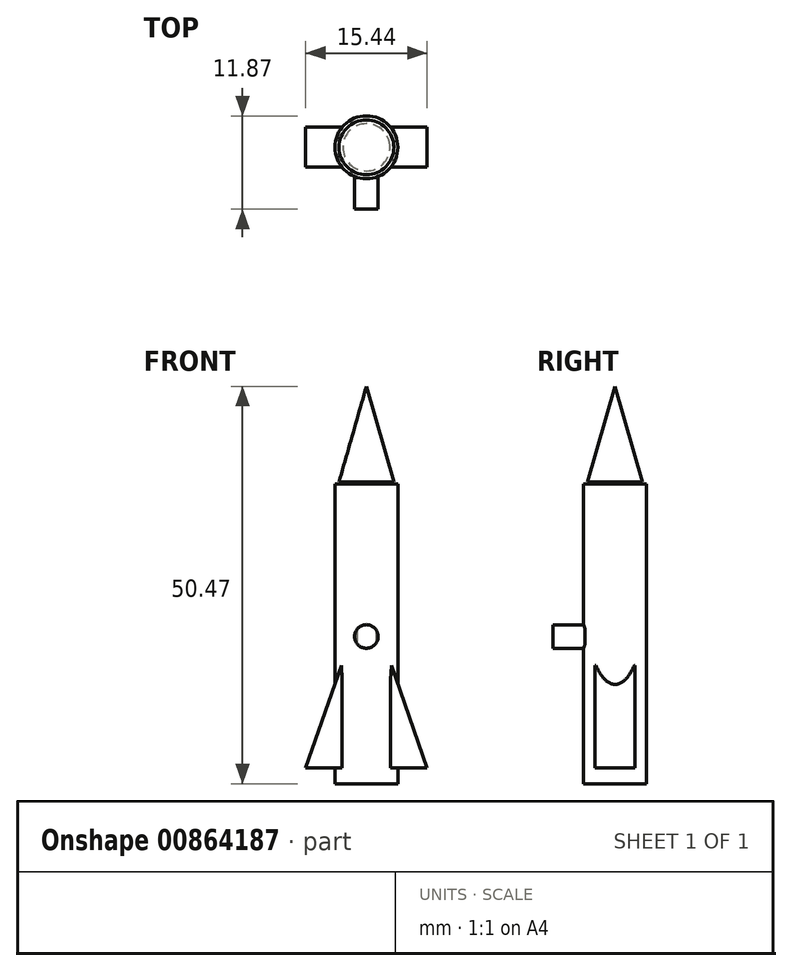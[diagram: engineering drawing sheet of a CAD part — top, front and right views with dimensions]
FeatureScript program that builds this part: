
annotation { "Feature Type Name" : "Feature", "Feature Type Description" : "" }
export const myFeature = defineFeature(function(context is Context, id is Id, definition is map)
    precondition{}
    {
        {
            var Q0;
            Q0=qCreatedBy(makeId("Top.planeOp"),FACE);
            var sketch = newSketch(context, id + "F0", { "sketchPlane" : qUnion([Q0])});
            skCircle(sketch, "E0", {"center": v(0, 0) * mm, "radius": 4 * mm});
            skSolve(sketch);
        }
        {
            var Q0;
            Q0=makeQuery(id+"F0.imprint","IMPRINT",FACE,{"disambiguationData":[TD([[makeQuery(id+"F0.imprint","IMPRINT",EDGE,{"derivedFrom":sQuery(id+"F0.wireOp",EDGE,"E0")}),1.0]])]});
            extrude(context, id + "F1", {"entities" : qUnion([Q0]), "depth" : 38.1 * mm, "offsetDistance" : 25.4 * mm});
        }
        {
            var Q0;
            Q0=qCreatedBy(makeId("Right.planeOp"),FACE);
            var sketch = newSketch(context, id + "F2", { "sketchPlane" : qUnion([Q0])});
            skLineSegment(sketch, "E1", {"start": v(0, 36.88) * mm, "end": v(3.48, 38.3) * mm});
            skLineSegment(sketch, "E2", {"start": v(3.48, 38.3) * mm, "end": v(0, 50.47) * mm});
            skLineSegment(sketch, "E3", {"start": v(0, 36.88) * mm, "end": v(0, 50.47) * mm});
            skSolve(sketch);
        }
        {
            var Q0;
            Q0=makeQuery(id+"F2.imprint","IMPRINT",FACE,{"disambiguationData":[TD([[makeQuery(id+"F2.imprint","IMPRINT",EDGE,{"derivedFrom":sQuery(id+"F2.wireOp",EDGE,"E1")}),1.0]])]});
            var Q1;
            Q1=sQuery(id+"F2.wireOp",EDGE,"E3");
            revolve(context, id + "F3", {"operationType" : NewBodyOperationType.ADD, "surfaceOperationType" : NewSurfaceOperationType.NEW, "entities" : qUnion([Q0]), "axis" : qUnion([Q1]), "revolveType" : RevolveType.FULL});
        }
        {
            var Q0;
            Q0=qCreatedBy(makeId("Front.planeOp"),FACE);
            var sketch = newSketch(context, id + "F4", { "sketchPlane" : qUnion([Q0])});
            skLineSegment(sketch, "E4", {"start": v(3.16, 15) * mm, "end": v(7.72, 2) * mm});
            skLineSegment(sketch, "E5", {"start": v(7.72, 2) * mm, "end": v(2.64, 2) * mm});
            skLineSegment(sketch, "E6", {"start": v(2.64, 2) * mm, "end": v(3.16, 15) * mm});
            skLineSegment(sketch, "E7.MirrorCS", {"start": v(-2.64, 2) * mm, "end": v(-3.16, 15) * mm});
            skLineSegment(sketch, "E8.MirrorCS", {"start": v(-3.16, 15) * mm, "end": v(-7.72, 2) * mm});
            skLineSegment(sketch, "E9.MirrorCS", {"start": v(-7.72, 2) * mm, "end": v(-2.64, 2) * mm});
            skSolve(sketch);
        }
        {
            var Q0;
            Q0=makeQuery(id+"F4.imprint","IMPRINT",FACE,{"disambiguationData":[TD([[makeQuery(id+"F4.imprint","IMPRINT",EDGE,{"derivedFrom":sQuery(id+"F4.wireOp",EDGE,"E7.MirrorCS")}),1.0]])]});
            var Q1;
            Q1=makeQuery(id+"F4.imprint","IMPRINT",FACE,{"disambiguationData":[TD([[makeQuery(id+"F4.imprint","IMPRINT",EDGE,{"derivedFrom":sQuery(id+"F4.wireOp",EDGE,"E4")}),-1.0]])]});
            extrude(context, id + "F5", {"entities" : qUnion([Q0, Q1]), "operationType" : NewBodyOperationType.ADD, "endBound" : BoundingType.SYMMETRIC, "depth" : 5.08 * mm, "offsetDistance" : 25.4 * mm});
        }
        {
            var Q0;
            Q0=qCreatedBy(makeId("Front.planeOp"),FACE);
            cPlane(context, id + "F6", {"entities" : qUnion([Q0]), "cplaneType" : CPlaneType.OFFSET, "offset" : 3.8 * mm, "width" : 152.4 * mm, "height" : 152.4 * mm});
        }
        {
            var Q0;
            Q0=qCreatedBy(id+"F6.planeOp",FACE);
            var sketch = newSketch(context, id + "F7", { "sketchPlane" : qUnion([Q0])});
            skCircle(sketch, "E10", {"center": v(0, 18.7) * mm, "radius": 1.5 * mm});
            skSolve(sketch);
        }
        {
            var Q0;
            Q0=makeQuery(id+"F7.imprint","IMPRINT",FACE,{"disambiguationData":[TD([[makeQuery(id+"F7.imprint","IMPRINT",EDGE,{"derivedFrom":sQuery(id+"F7.wireOp",EDGE,"E10")}),1.0]])]});
            extrude(context, id + "F8", {"entities" : qUnion([Q0]), "operationType" : NewBodyOperationType.ADD, "depth" : 4.06 * mm, "offsetDistance" : 25.4 * mm});
        }
    });
